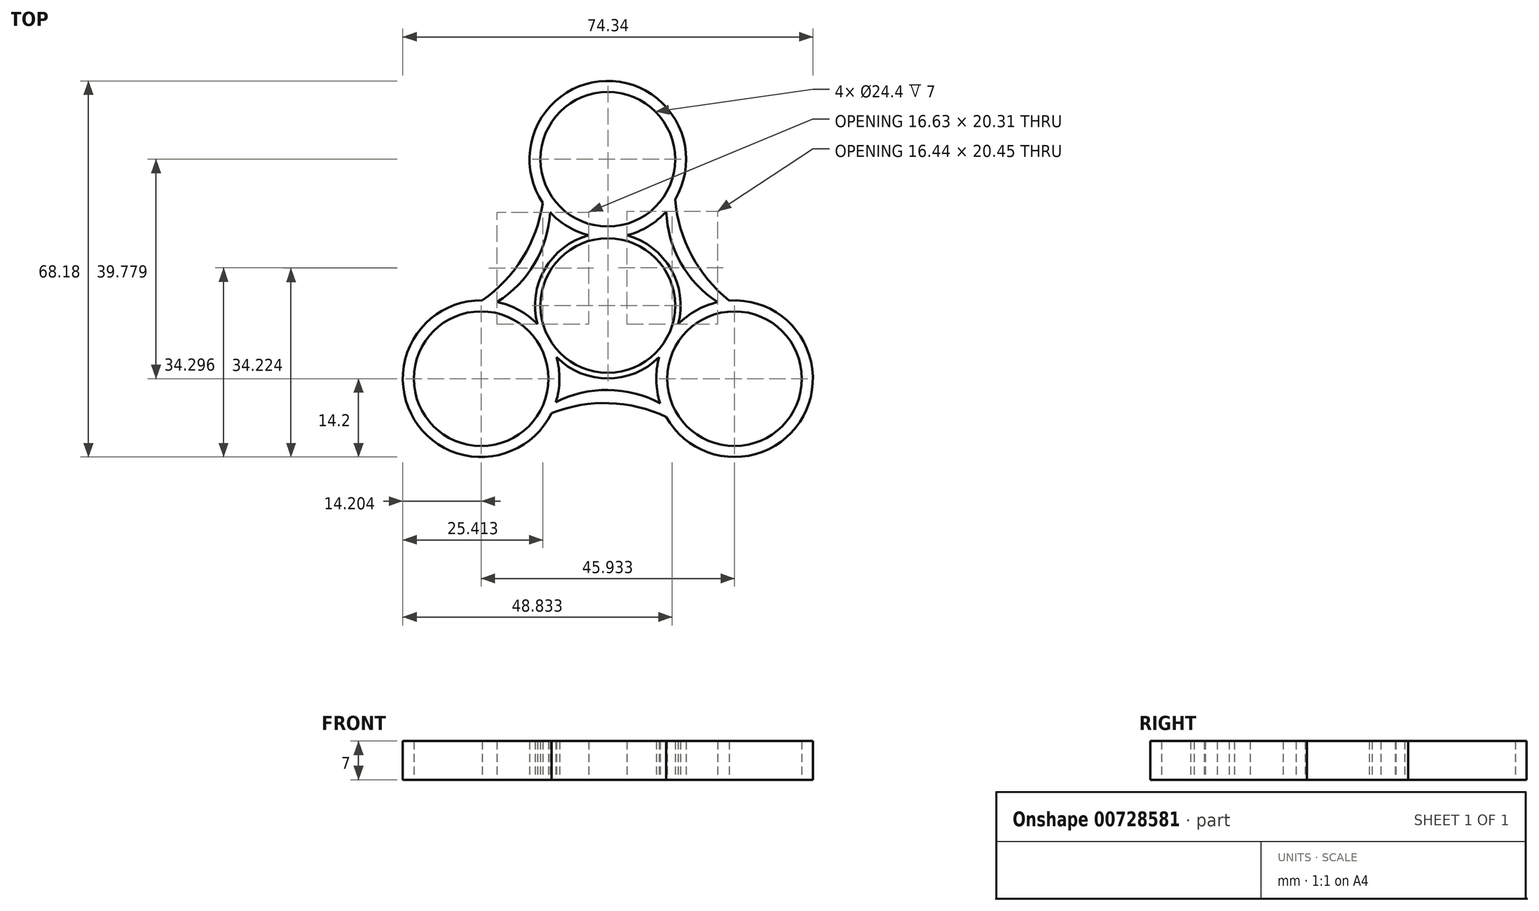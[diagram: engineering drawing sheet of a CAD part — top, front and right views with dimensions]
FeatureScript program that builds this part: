
annotation { "Feature Type Name" : "Feature", "Feature Type Description" : "" }
export const myFeature = defineFeature(function(context is Context, id is Id, definition is map)
    precondition{}
    {
        {
            var Q0;
            Q0=qCreatedBy(makeId("Top.planeOp"),FACE);
            var sketch = newSketch(context, id + "F0", { "sketchPlane" : qUnion([Q0])});
            skCircle(sketch, "E0", {"center": v(0, 0) * mm, "radius": 12.2 * mm});
            skCircle(sketch, "E1", {"center": v(0, 26.52) * mm, "radius": 12.2 * mm});
            skCircle(sketch, "E2.1.0", {"center": v(-22.97, -13.26) * mm, "radius": 12.2 * mm});
            skCircle(sketch, "E2.2.0", {"center": v(22.97, -13.26) * mm, "radius": 12.2 * mm});
            skArc(sketch, "E3", {"start": v(-3.44, 12.74) * mm, "mid": v(-11.43, 6.6) * mm, "end": v(-12.76, -3.39) * mm});
            skArc(sketch, "E4", {"start": v(3.44, 12.74) * mm, "mid": v(0, 40.72) * mm, "end": v(-3.44, 12.74) * mm});
            skArc(sketch, "E5.1.0", {"start": v(-12.76, -3.39) * mm, "mid": v(-35.26, -20.36) * mm, "end": v(-9.31, -9.35) * mm});
            skArc(sketch, "E5.2.0", {"start": v(9.31, -9.35) * mm, "mid": v(35.26, -20.36) * mm, "end": v(12.76, -3.39) * mm});
            skArc(sketch, "E6.trimOffspring", {"start": v(-9.31, -9.35) * mm, "mid": v(0, -13.2) * mm, "end": v(9.31, -9.35) * mm});
            skArc(sketch, "E7.trimOffspring", {"start": v(12.76, -3.39) * mm, "mid": v(11.43, 6.6) * mm, "end": v(3.44, 12.74) * mm});
            skArc(sketch, "E8", {"start": v(-20.07, 0.64) * mm, "mid": v(-13.28, 7.6) * mm, "end": v(-10.46, 16.92) * mm});
            skArc(sketch, "E9", {"start": v(-22.77, 0.94) * mm, "mid": v(-15.44, 8.64) * mm, "end": v(-11.8, 18.62) * mm});
            skArc(sketch, "E10.1.0", {"start": v(10.57, -20.18) * mm, "mid": v(0.24, -17.7) * mm, "end": v(-10.22, -19.53) * mm});
            skArc(sketch, "E10.1.1", {"start": v(9.48, -17.7) * mm, "mid": v(0.05, -15.3) * mm, "end": v(-9.42, -17.52) * mm});
            skArc(sketch, "E10.2.0", {"start": v(12.2, 19.25) * mm, "mid": v(15.2, 9.05) * mm, "end": v(22.02, 0.9) * mm});
            skArc(sketch, "E10.2.1", {"start": v(10.6, 17.06) * mm, "mid": v(13.23, 7.7) * mm, "end": v(19.88, 0.6) * mm});
            skSolve(sketch);
        }
        {
            var Q0;
            Q0=qSketchRegion(id+"F0",true);
            extrude(context, id + "F1", {"entities" : qUnion([Q0]), "depth" : 7 * mm, "offsetDistance" : 25 * mm});
        }
    });
